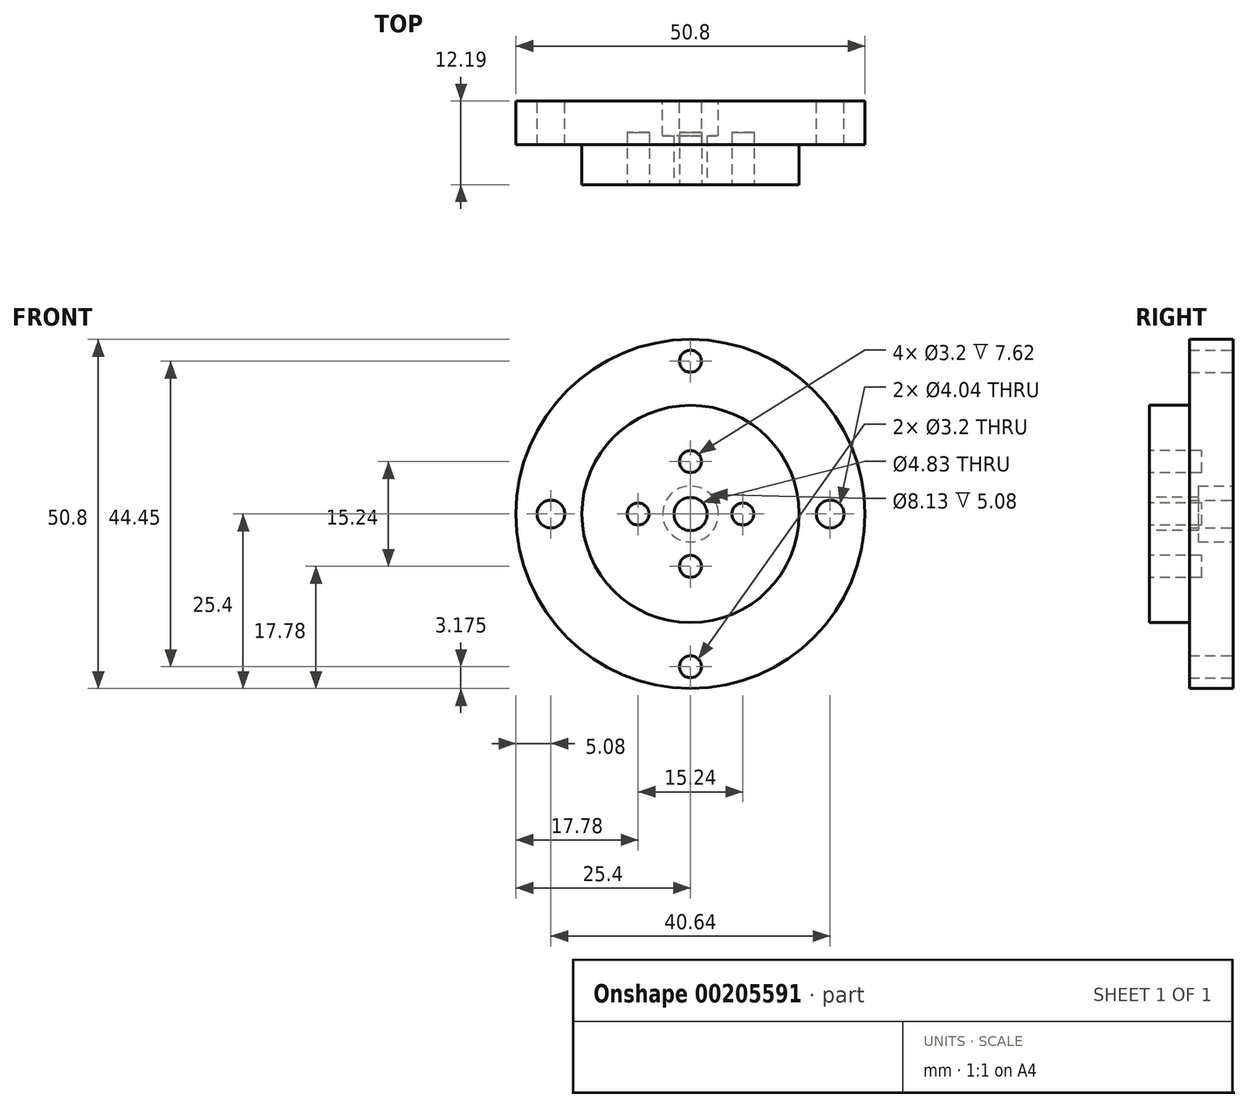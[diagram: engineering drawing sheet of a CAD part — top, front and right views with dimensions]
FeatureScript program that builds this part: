
annotation { "Feature Type Name" : "Feature", "Feature Type Description" : "" }
export const myFeature = defineFeature(function(context is Context, id is Id, definition is map)
    precondition{}
    {
        {
            var Q0;
            Q0=qCreatedBy(makeId("Front.planeOp"),FACE);
            var sketch = newSketch(context, id + "F0", { "sketchPlane" : qUnion([Q0])});
            skCircle(sketch, "E0", {"center": v(0, 0) * mm, "radius": 25.4 * mm});
            skSolve(sketch);
        }
        {
            var Q0;
            Q0=qSketchRegion(id+"F0",true);
            extrude(context, id + "F1", {"entities" : qUnion([Q0]), "depth" : 6.35 * mm});
        }
        {
            var Q0;
            Q0=makeQuery(id+"F1.opExtrude","CAP_FACE",FACE,{"disambiguationData":[OSD([sQuery(id+"F0.wireOp",EDGE,"E0")])],"isStart":false});
            var sketch = newSketch(context, id + "F2", { "sketchPlane" : qUnion([Q0])});
            skCircle(sketch, "E1", {"center": v(0, 0) * mm, "radius": 15.81 * mm});
            skSolve(sketch);
        }
        {
            var Q0;
            Q0=qSketchRegion(id+"F2",true);
            extrude(context, id + "F3", {"entities" : qUnion([Q0]), "operationType" : NewBodyOperationType.ADD, "depth" : 5.84 * mm});
        }
        {
            var Q0;
            Q0=makeQuery(id+"F3.opExtrude","CAP_FACE",FACE,{"disambiguationData":[OSD([sQuery(id+"F2.wireOp",EDGE,"E1")])],"isStart":false});
            var sketch = newSketch(context, id + "F4", { "sketchPlane" : qUnion([Q0])});
            skCircle(sketch, "E2", {"center": v(7.62, 0) * mm, "radius": 1.6 * mm});
            skCircle(sketch, "E3", {"center": v(0, 7.62) * mm, "radius": 1.6 * mm});
            skCircle(sketch, "E4", {"center": v(-7.62, 0) * mm, "radius": 1.6 * mm});
            skCircle(sketch, "E5", {"center": v(0, -7.62) * mm, "radius": 1.6 * mm});
            skCircle(sketch, "E6", {"center": v(0, 0) * mm, "radius": 2.41 * mm});
            skSolve(sketch);
        }
        {
            var Q0;
            Q0=qSketchRegion(id+"F4",true);
            extrude(context, id + "F5", {"entities" : qUnion([Q0]), "operationType" : NewBodyOperationType.REMOVE, "oppositeDirection" : true, "depth" : 7.62 * mm});
        }
        {
            var Q0;
            Q0=makeQuery(id+"F1.opExtrude","CAP_FACE",FACE,{"disambiguationData":[OSD([sQuery(id+"F0.wireOp",EDGE,"E0")])],"isStart":true});
            var sketch = newSketch(context, id + "F6", { "sketchPlane" : qUnion([Q0])});
            skCircle(sketch, "E7", {"center": v(0, 0) * mm, "radius": 4.06 * mm});
            skSolve(sketch);
        }
        {
            var Q0;
            Q0=qSketchRegion(id+"F6",true);
            extrude(context, id + "F7", {"entities" : qUnion([Q0]), "operationType" : NewBodyOperationType.REMOVE, "oppositeDirection" : true, "depth" : 5.08 * mm});
        }
        {
            var Q0;
            Q0=makeQuery(id+"F1.opExtrude","CAP_FACE",FACE,{"disambiguationData":[OSD([sQuery(id+"F0.wireOp",EDGE,"E0")])],"isStart":true});
            var sketch = newSketch(context, id + "F8", { "sketchPlane" : qUnion([Q0])});
            skCircle(sketch, "E8", {"center": v(0, 22.23) * mm, "radius": 1.6 * mm});
            skCircle(sketch, "E9", {"center": v(20.32, 0) * mm, "radius": 2.02 * mm});
            skCircle(sketch, "E10", {"center": v(0, -22.23) * mm, "radius": 1.6 * mm});
            skCircle(sketch, "E11", {"center": v(-20.32, 0) * mm, "radius": 2.02 * mm});
            skSolve(sketch);
        }
        {
            var Q0;
            Q0=qSketchRegion(id+"F8",true);
            extrude(context, id + "F9", {"entities" : qUnion([Q0]), "operationType" : NewBodyOperationType.REMOVE, "endBound" : BoundingType.THROUGH_ALL, "oppositeDirection" : true, "depth" : 25.4 * mm});
        }
    });
